# Revit family: Central digital para deteccion de gas_Aguilera Electronica
name_source: partatom
category: Dispositivos de alarma de incendios
units: mm (PartAtom-declared; Revit-internal decimal feet)

## family parameters
Anfitrión = Cara
Compartido = No
Corte con vacíos al cargar = No
Cota de conector redondo = Diámetro de uso
Mantener orientación de anotación = Sí
Número OmniClass = 23.85.30.21.11.17
Punto de cálculo de habitación = No
Tipo de pieza = Normal
Título OmniClass = Other Components

## types (2) — shared parameters
Alto = 153 mm  [stored 0.501969 ft]
Ancho = 202 mm  [stored 0.66273 ft]
Elevación por defecto = 1200 mm
Fabricante = Aguilera Electrónica
Fondo = 86 mm  [stored 0.282152 ft]
Símbolo = Sí
Símbolo texto modelo = Sí
URL = https://aguilera.es

## per-type parameters (varying)
| type | Descripción | Modelo |
| Central digital de 3 zonas para detección de gas con display | Central digital de gas para tres sensores 4-20mA catalíticos o pellistor de gas inflamable y/o monóxido de carbono como máximo. Montaje en pared. Dispone de display donde se muestra el porcentaje de la concentración del gas detectado en tiempo real para cada sensor.
Provista de 3 relés de alarma configurables para distintas concentraciones del LEL para gases inflamables o ppm para CO y un relé de avería. Dispone de función de TEST y RESET. Entrada auxiliar para alarma manual o electroválvula con sensor magnético.
Alimentación 230 Vca 10VA / 24Vcc 12W
Dimensiones: 202 x 153 x 86, IP65
Sensores admitidos:
Familia AE/GI-ST441 y AE/GI-ST193. Metano y/o GLP, rango de 0 ÷20% LEL
Familia AE/GI-TS282 y AE/GI-TS293 Catalítico gas inflamable, rango de 0 ÷20% LEL
Familia AE/GI-TS282 y AE/GI-TS293 Pellistor gas inflamable, rango de 0 ÷100% LEL
Detectores AE/GI-TS282ECS y AE/GI-TS293ECS electroquímicos de CO, rango de 0 ÷300 ppm | AE/GI-CTP25 |
| Central digital de 4 zonas para detección de gas con display | Central digital de gas para cuatro sensores 4-20mA catalíticos o pellistor de gas inflamable como máximo. Montaje en pared. Dispone de display donde se muestra el porcentaje de la concentración del gas detectado en tiempo real para cada sensor.
Provista de 2 relés de alarma configurables para 10-20% LEL y 20-30 % LEL respectivamente y un relé de avería. Dispone de función de TEST y RESET. Entrada auxiliar para alarma manual o electroválvula con sensor magnético.
Alimentación 230 Vca 10VA / 24Vcc 12W
Dimensiones: 202 x 153 x 86, IP65
Sensores admitidos:
Familia AE/GI-ST441 y AE/GI-ST193. Metano y/o GLP, rango de 0 ÷20% LEL
Familia AE/GI-TS282 y AE/GI-TS293 Catalítico gas inflamable, rango de 0 ÷20% LEL
Familia AE/GI-TS282 y AE/GI-TS293 Pellistor gas inflamable, rango de 0 ÷100% LEL | AE/GI-CTP24 |

note: [stored X ft] marks values corroborated as IEEE doubles in the binary element streams (Revit-internal decimal feet)
